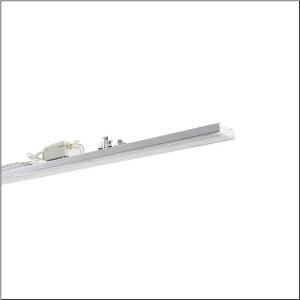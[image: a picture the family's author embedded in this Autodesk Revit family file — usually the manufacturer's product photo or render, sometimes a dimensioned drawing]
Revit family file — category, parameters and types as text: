
# Revit family: licross_r__21_recessed_ho_52tl18cn4c5m_5c60
name_source: partatom
category: Lighting Fixtures
units: mm (PartAtom-declared; Revit-internal decimal feet)

## family parameters
Cut with Voids When Loaded = No
Host = Face
Light Source = No
Part Type = Normal
Room Calculation Point = No
Round Connector Dimension = Use Diameter
Shared = No

## types (1)
- --- (1 x LED, 12540 lm, 68.4 W, 4000K)
    Apparent Load = 68 VA
    CIE Flux Codes = 75 94 99 100 100
    Color Rendering = 80
    Color Temperature = 4000K
    Default Elevation = 1800 mm
    Description = Licross® 21 Recessed HO, luminaire insert, of sheet steel, galvanised, coil coated, white, length: 1.500mm, width: 66mm, height: 67mm, LED rated luminous flux: 12.540lm, light colour: 840, control gear: ON/OFF Multilumen, CLOi, control gear: ECG Multilumen, with plug, 3-pole, with phase selection, mains connection: 220..240V, AC, 50/60Hz, halogen-free wiring, primary light control with lens, of plastic, primary optical cover: cover, of PMMA, light emission: direct distribution, primary light characteristic: symmetric, protection rating (complete): IP40, insulation class (complete): insulation class I (protective earthing), certification: CE, ENEC, VDE, UKCA, protection symbol: D if used in an environment without relevant dust loads with corresponding accessories, impact resistance: IK06, permissible ambient temperature for indoor applications: -35..+30°C, corresponds to IFS (International Featured Standards) requirements for safety and quality in the food industry, reducing of maximum allowable ambient temperature of 5°C with ceiling mounting, LABS conformity tested according to VDMA 24364:2018-05, packaging unit: 1 piece
    Height = 58 mm
    Lamp = 1 x LED
    Lamp Light Flux = 12540 lm
    Lamp Power = 68.4 W
    Lamp count = 1
    Length = 1500 mm
    Luminous efficacy = 183 lm/W
    Manufacturer = Siteco
    ModVariant = No
    Model = 52TL18CN4C5M
    Mounting Place = Ceiling
    Mounting Type = Pendant
    Number of Poles = 1
    OnlyDefault = Yes
    Power Factor = 1
    Product Name = Licross® 21 Recessed HO
    Product group = luminaire insert
    ProductGroupID = 901
    Protection Class = Protection class I
    Protection Degree = IP 40
    RLX_Detail_Level = 1
    RLX_Emergency_Light_Flux = 0 lm
    RLX_Emergency_Type = 0
    RLX_Emergency_Type_DB = No
    RlxData = <blob elided: 22309 chars, md5=0a0bdad5>
    Socket = socket
    Standby Power = 0 W
    System Light Flux = 12540 lm
    System Power = 68 W
    Type Comments = factory setting: luminous flux: 100 % | (A | C | E) | 161 mA
    Type Image = l_1296930.jpg
    URL = http://relux.com
    VarID = @adj_040129
    Voltage = 0 V
    Weight = 0.00 kg
    Width = 66 mm

## geometry (parser evidence)
native form markers: Blend x4, Sweep x11
no freeform markers — native parametric forms only
